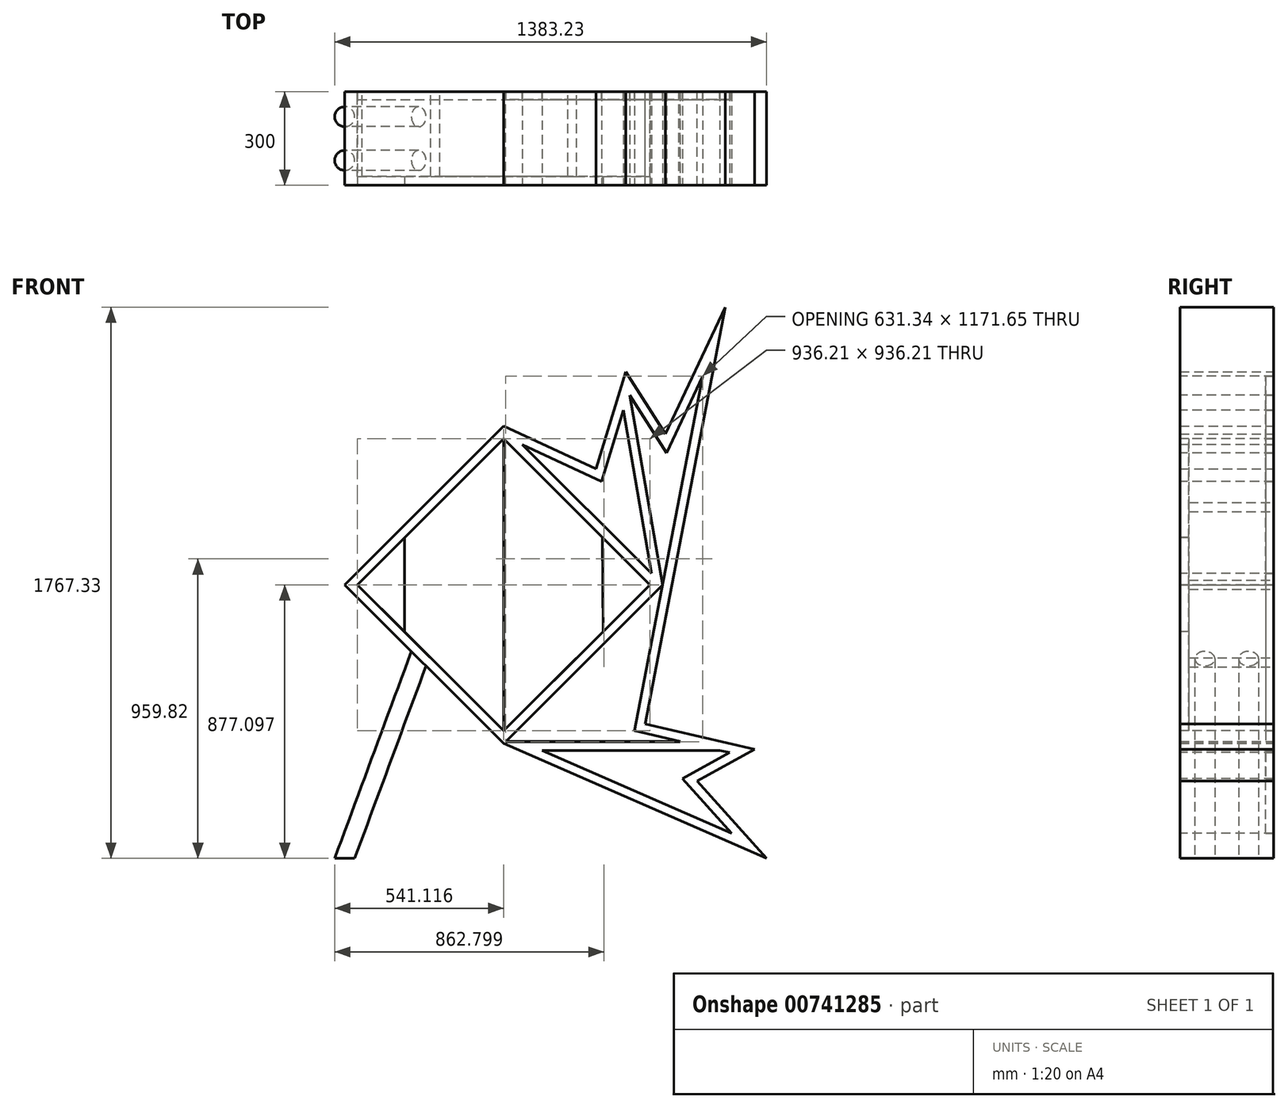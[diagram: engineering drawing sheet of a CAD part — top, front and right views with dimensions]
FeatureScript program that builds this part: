
annotation { "Feature Type Name" : "Feature", "Feature Type Description" : "" }
export const myFeature = defineFeature(function(context is Context, id is Id, definition is map)
    precondition{}
    {
        {
            var Q0;
            Q0=qCreatedBy(makeId("Front.planeOp"),FACE);
            var sketch = newSketch(context, id + "F0", { "sketchPlane" : qUnion([Q0])});
            skLineSegment(sketch, "E0", {"start": v(-825.73, 89.76) * mm, "end": v(-316.61, 598.87) * mm});
            skLineSegment(sketch, "E1", {"start": v(192.5, 89.76) * mm, "end": v(-316.61, -419.36) * mm});
            skLineSegment(sketch, "E2", {"start": v(-316.61, -419.36) * mm, "end": v(-825.73, 89.76) * mm});
            skLineSegment(sketch, "E3", {"start": v(-316.61, 598.87) * mm, "end": v(-21.16, 461.1) * mm});
            skLineSegment(sketch, "E4", {"start": v(-21.16, 461.1) * mm, "end": v(74.16, 772.86) * mm});
            skLineSegment(sketch, "E5", {"start": v(74.16, 772.86) * mm, "end": v(201.44, 572.46) * mm});
            skLineSegment(sketch, "E6", {"start": v(145.6, -358.84) * mm, "end": v(487.14, -437.47) * mm});
            skLineSegment(sketch, "E7", {"start": v(487.14, -437.47) * mm, "end": v(302.49, -539.98) * mm});
            skLineSegment(sketch, "E8", {"start": v(302.49, -539.98) * mm, "end": v(525.5, -787.34) * mm});
            skLineSegment(sketch, "E9", {"start": v(-316.61, -419.36) * mm, "end": v(525.5, -787.34) * mm});
            skPoint(sketch, "E10.endSnap0", {"position": v(394.81, -488.72) * mm});
            skLineSegment(sketch, "E11", {"start": v(-825.73, 89.76) * mm, "end": v(-588.14, -147.83) * mm});
            skLineSegment(sketch, "E12", {"start": v(-825.73, 89.76) * mm, "end": v(-825.73, -787.34) * mm, "construction": true});
            skLineSegment(sketch, "E13", {"start": v(-566.21, -86.45) * mm, "end": v(-825.73, -787.34) * mm});
            skLineSegment(sketch, "E14", {"start": v(-784.72, 89.76) * mm, "end": v(-316.61, 557.86) * mm});
            skLineSegment(sketch, "E15", {"start": v(-316.61, 557.86) * mm, "end": v(151.5, 89.76) * mm});
            skLineSegment(sketch, "E16", {"start": v(-784.72, 89.76) * mm, "end": v(-316.61, -378.35) * mm});
            skLineSegment(sketch, "E17", {"start": v(-316.61, -378.35) * mm, "end": v(151.5, 89.76) * mm});
            skLineSegment(sketch, "E18", {"start": v(-256.66, 538.92) * mm, "end": v(-3.18, 420.72) * mm});
            skLineSegment(sketch, "E19", {"start": v(66.34, 648.1) * mm, "end": v(-3.18, 420.72) * mm});
            skLineSegment(sketch, "E20", {"start": v(156.9, 125.36) * mm, "end": v(66.34, 648.1) * mm});
            skLineSegment(sketch, "E21", {"start": v(392.79, 979.99) * mm, "end": v(136.4, -356.72) * mm});
            skLineSegment(sketch, "E22", {"start": v(201.44, 572.46) * mm, "end": v(392.79, 979.99) * mm});
            skPoint(sketch, "E23.startSnap0", {"position": v(297.11, 776.23) * mm});
            skLineSegment(sketch, "E24", {"start": v(205.26, 512.36) * mm, "end": v(320.74, 758.3) * mm});
            skLineSegment(sketch, "E25", {"start": v(320.74, 758.3) * mm, "end": v(102.46, -379.66) * mm});
            skLineSegment(sketch, "E26", {"start": v(407.01, -448.78) * mm, "end": v(256.54, -532.32) * mm});
            skLineSegment(sketch, "E27", {"start": v(256.54, -532.32) * mm, "end": v(414, -706.97) * mm});
            skPoint(sketch, "E27.endSnap0", {"position": v(414, -663.66) * mm});
            skLineSegment(sketch, "E28", {"start": v(87.04, 698.48) * mm, "end": v(192.5, 89.76) * mm});
            skLineSegment(sketch, "E29", {"start": v(-316.61, 598.87) * mm, "end": v(192.5, 89.76) * mm});
            skLineSegment(sketch, "E30", {"start": v(136.4, -356.72) * mm, "end": v(487.14, -437.47) * mm});
            skLineSegment(sketch, "E31", {"start": v(87.04, 698.48) * mm, "end": v(205.26, 512.36) * mm});
            skLineSegment(sketch, "E32", {"start": v(-301.62, -404.37) * mm, "end": v(-310.6, -413.34) * mm});
            skLineSegment(sketch, "E33", {"start": v(-310.6, -413.34) * mm, "end": v(248.8, -413.34) * mm});
            skLineSegment(sketch, "E34", {"start": v(102.46, -379.66) * mm, "end": v(248.8, -413.34) * mm});
            skLineSegment(sketch, "E35", {"start": v(379.97, -442.55) * mm, "end": v(-191.11, -442.55) * mm});
            skLineSegment(sketch, "E36", {"start": v(379.97, -442.55) * mm, "end": v(407.01, -448.78) * mm});
            skLineSegment(sketch, "E37", {"start": v(-191.11, -442.55) * mm, "end": v(414, -706.97) * mm});
            skSolve(sketch);
        }
        {
            var Q0;
            {var subQ1=sQuery(id+"F0.wireOp",EDGE,"E3");Q0=makeQuery(id+"F0.imprint","IMPRINT",FACE,{"disambiguationData":[TD([[makeQuery(id+"F0.imprint","IMPRINT",EDGE,{"derivedFrom":subQ1}),-1.0]])]});}
            var Q1;
            {var subQ1=sQuery(id+"F0.wireOp",EDGE,"E0");Q1=makeQuery(id+"F0.imprint","IMPRINT",FACE,{"disambiguationData":[TD([[makeQuery(id+"F0.imprint","IMPRINT",EDGE,{"derivedFrom":subQ1}),-1.0]])]});}
            var Q2;
            Q2=makeQuery(id+"F0.imprint","IMPRINT",FACE,{"disambiguationData":[TD([[makeQuery(id+"F0.imprint","IMPRINT",EDGE,{"derivedFrom":sQuery(id+"F0.wireOp",EDGE,"E14")}),-1.0]])]});
            var Q3;
            {var subQ0=sQuery(id+"F0.wireOp",EDGE,"E24");Q3=makeQuery(id+"F0.imprint","IMPRINT",FACE,{"disambiguationData":[TD([[makeQuery(id+"F0.imprint","IMPRINT",EDGE,{"derivedFrom":subQ0}),-1.0]])]});}
            var Q4;
            Q4=makeQuery(id+"F0.imprint","IMPRINT",FACE,{"disambiguationData":[TD([[makeQuery(id+"F0.imprint","IMPRINT",EDGE,{"derivedFrom":sQuery(id+"F0.wireOp",EDGE,"E26")}),-1.0]])]});
            var Q5;
            {var subQ4=sQuery(id+"F0.wireOp",EDGE,"E32");Q5=makeQuery(id+"F0.imprint","IMPRINT",FACE,{"disambiguationData":[TD([[makeQuery(id+"F0.imprint","IMPRINT",EDGE,{"derivedFrom":subQ4}),1.0]])]});}
            var Q6;
            {var subQ0=sQuery(id+"F0.wireOp",EDGE,"E18");Q6=makeQuery(id+"F0.imprint","IMPRINT",FACE,{"disambiguationData":[TD([[makeQuery(id+"F0.imprint","IMPRINT",EDGE,{"derivedFrom":subQ0}),-1.0]])]});}
            extrude(context, id + "F1", {"entities" : qUnion([Q0, Q1, Q2, Q3, Q4, Q5, Q6]), "depth" : 300 * mm, "offsetDistance" : 25 * mm});
        }
        {
            var Q0;
            Q0=makeQuery(id+"F1.opExtrude","CAP_FACE",FACE,{"disambiguationData":[OSD([sQuery(id+"F0.wireOp",EDGE,"E0"),sQuery(id+"F0.wireOp",EDGE,"E2"),sQuery(id+"F0.wireOp",EDGE,"E3"),sQuery(id+"F0.wireOp",EDGE,"E4"),sQuery(id+"F0.wireOp",EDGE,"E5"),sQuery(id+"F0.wireOp",EDGE,"E7"),sQuery(id+"F0.wireOp",EDGE,"E8"),sQuery(id+"F0.wireOp",EDGE,"E9"),sQuery(id+"F0.wireOp",EDGE,"E11"),sQuery(id+"F0.wireOp",EDGE,"E21"),sQuery(id+"F0.wireOp",EDGE,"E22"),sQuery(id+"F0.wireOp",EDGE,"E30")])],"isStart":false});
            var sketch = newSketch(context, id + "F2", { "sketchPlane" : qUnion([Q0])});
            skLineSegment(sketch, "E38", {"start": v(-784.72, 89.76) * mm, "end": v(-316.61, 557.86) * mm});
            skLineSegment(sketch, "E39", {"start": v(-784.72, 89.76) * mm, "end": v(-316.61, -378.35) * mm});
            skLineSegment(sketch, "E40", {"start": v(-316.61, -378.35) * mm, "end": v(151.5, 89.76) * mm});
            skLineSegment(sketch, "E41", {"start": v(-316.61, 557.86) * mm, "end": v(151.5, 89.76) * mm});
            skPoint(sketch, "E42.startSnap0", {"position": v(-168.89, 529.99) * mm});
            skLineSegment(sketch, "E43", {"start": v(-3.18, 420.72) * mm, "end": v(66.5, 648.65) * mm});
            skLineSegment(sketch, "E44", {"start": v(-256.66, 538.92) * mm, "end": v(-3.18, 420.72) * mm});
            skLineSegment(sketch, "E45", {"start": v(66.5, 648.65) * mm, "end": v(156.84, 125.43) * mm});
            skLineSegment(sketch, "E46", {"start": v(87.44, 697.85) * mm, "end": v(192.44, 89.7) * mm});
            skLineSegment(sketch, "E47", {"start": v(-256.66, 538.92) * mm, "end": v(156.84, 125.43) * mm});
            skLineSegment(sketch, "E48", {"start": v(87.44, 697.85) * mm, "end": v(205.26, 512.36) * mm});
            skLineSegment(sketch, "E49", {"start": v(205.26, 512.36) * mm, "end": v(320.74, 758.3) * mm});
            skLineSegment(sketch, "E50", {"start": v(192.44, 89.7) * mm, "end": v(-309.57, -412.31) * mm});
            skLineSegment(sketch, "E51", {"start": v(102.64, -378.71) * mm, "end": v(320.74, 758.3) * mm});
            skLineSegment(sketch, "E52", {"start": v(-193.95, -441.31) * mm, "end": v(375.58, -441.31) * mm});
            skLineSegment(sketch, "E53", {"start": v(-310.6, -412.25) * mm, "end": v(-310.27, -412.25) * mm});
            skLineSegment(sketch, "E54", {"start": v(102.64, -378.71) * mm, "end": v(248.61, -412.31) * mm});
            skLineSegment(sketch, "E55", {"start": v(-309.57, -412.31) * mm, "end": v(248.61, -412.31) * mm});
            skLineSegment(sketch, "E56", {"start": v(375.58, -441.31) * mm, "end": v(407.3, -448.62) * mm});
            skLineSegment(sketch, "E57", {"start": v(407.3, -448.62) * mm, "end": v(256.54, -532.32) * mm});
            skLineSegment(sketch, "E58", {"start": v(414, -706.97) * mm, "end": v(256.54, -532.32) * mm});
            skLineSegment(sketch, "E59", {"start": v(414, -706.97) * mm, "end": v(-193.95, -441.31) * mm});
            skSolve(sketch);
        }
        {
            var Q0;
            Q0 = qSketchRegion(id + "F2", true);
            extrude(context, id + "F3", {"entities" : qUnion([Q0]), "operationType" : NewBodyOperationType.REMOVE, "endBound" : BoundingType.THROUGH_ALL, "oppositeDirection" : true, "depth" : 250 * mm, "offsetDistance" : 25 * mm});
        }
        {
            var Q0;
            Q0=makeQuery(id+"F2.imprint","IMPRINT",FACE,{"disambiguationData":[TD([[makeQuery(id+"F2.imprint","IMPRINT",EDGE,{"derivedFrom":sQuery(id+"F2.wireOp",EDGE,"E38")}),1.0]])]});
            var sketch = newSketch(context, id + "F4", { "sketchPlane" : qUnion([Q0])});
            skLineSegment(sketch, "E60", {"start": v(-316.61, 557.86) * mm, "end": v(-316.61, -378.35) * mm});
            skLineSegment(sketch, "E61", {"start": v(-634.72, 239.76) * mm, "end": v(-634.72, -60.25) * mm});
            skLineSegment(sketch, "E62", {"start": v(0, 241.25) * mm, "end": v(1.5, -60.24) * mm});
            skLineSegment(sketch, "E63", {"start": v(-634.72, 239.76) * mm, "end": v(-784.72, 89.76) * mm});
            skLineSegment(sketch, "E64", {"start": v(-784.72, 89.76) * mm, "end": v(-634.72, -60.25) * mm});
            skLineSegment(sketch, "E65", {"start": v(0, 241.25) * mm, "end": v(151.5, 89.76) * mm});
            skLineSegment(sketch, "E66", {"start": v(151.5, 89.76) * mm, "end": v(1.5, -60.24) * mm});
            skLineSegment(sketch, "E67", {"start": v(-634.72, 239.76) * mm, "end": v(-316.61, 557.86) * mm});
            skLineSegment(sketch, "E68", {"start": v(0, 241.25) * mm, "end": v(-316.61, 557.86) * mm});
            skLineSegment(sketch, "E69", {"start": v(1.5, -60.24) * mm, "end": v(-316.61, -378.35) * mm});
            skLineSegment(sketch, "E70", {"start": v(-634.72, -60.25) * mm, "end": v(-316.61, -378.35) * mm});
            skSolve(sketch);
        }
        {
            var Q0;
            Q0=makeQuery(id+"F4.imprint","IMPRINT",FACE,{"disambiguationData":[TD([[makeQuery(id+"F4.imprint","IMPRINT",EDGE,{"derivedFrom":sQuery(id+"F4.wireOp",EDGE,"E60")}),-1.0]])]});
            var Q1;
            Q1=makeQuery(id+"F4.imprint","IMPRINT",FACE,{"disambiguationData":[TD([[makeQuery(id+"F4.imprint","IMPRINT",EDGE,{"derivedFrom":sQuery(id+"F4.wireOp",EDGE,"E62")}),1.0]])]});
            extrude(context, id + "F5", {"entities" : qUnion([Q0, Q1]), "oppositeDirection" : true, "depth" : 29 * mm, "offsetDistance" : 25 * mm});
        }
        {
            var Q0;
            Q0=qCreatedBy(makeId("Top.planeOp"),FACE);
            var sketch = newSketch(context, id + "F6", { "sketchPlane" : qUnion([Q0])});
            skLineSegment(sketch, "E71.bottom", {"start": v(411.08, 500.96) * mm, "end": v(525.5, 500.96) * mm});
            skLineSegment(sketch, "E71.top", {"start": v(411.08, 415.79) * mm, "end": v(525.5, 415.79) * mm});
            skLineSegment(sketch, "E71.left", {"start": v(411.08, 500.96) * mm, "end": v(411.08, 415.79) * mm});
            skLineSegment(sketch, "E71.right", {"start": v(525.5, 500.96) * mm, "end": v(525.5, 415.79) * mm});
            skSolve(sketch);
        }
        {
            var Q0;
            Q0 = qSketchRegion(id + "F6", true);
            extrude(context, id + "F7", {"entities" : qUnion([Q0]), "oppositeDirection" : true, "depth" : 787.34 * mm, "offsetDistance" : 25 * mm});
        }
        {
            var Q0;
            Q0=makeQuery(id+"F7.opExtrude","CAP_FACE",FACE,{"disambiguationData":[OSD([sQuery(id+"F6.wireOp",EDGE,"E71.bottom"),sQuery(id+"F6.wireOp",EDGE,"E71.top"),sQuery(id+"F6.wireOp",EDGE,"E71.left"),sQuery(id+"F6.wireOp",EDGE,"E71.right")])],"isStart":false});
            var sketch = newSketch(context, id + "F8", { "sketchPlane" : qUnion([Q0])});
            skLineSegment(sketch, "E72", {"start": v(-825.73, 300) * mm, "end": v(-825.73, 0) * mm, "construction": true});
            skCircle(sketch, "E73", {"center": v(-825.73, 220) * mm, "radius": 32 * mm});
            skLineSegment(sketch, "E74", {"start": v(-825.73, 220) * mm, "end": v(-604.76, 220) * mm, "construction": true});
            skCircle(sketch, "E75", {"center": v(-825.73, 80) * mm, "radius": 32 * mm});
            skLineSegment(sketch, "E76", {"start": v(-825.73, 80) * mm, "end": v(-600.47, 80) * mm, "construction": true});
            skSolve(sketch);
        }
        {
            var Q0;
            Q0=makeQuery(id+"F8.imprint","IMPRINT",FACE,{"disambiguationData":[TD([[makeQuery(id+"F8.imprint","IMPRINT",EDGE,{"derivedFrom":sQuery(id+"F8.wireOp",EDGE,"E73")}),1.0]])]});
            var Q1;
            Q1=makeQuery(id+"F8.imprint","IMPRINT",FACE,{"disambiguationData":[TD([[makeQuery(id+"F8.imprint","IMPRINT",EDGE,{"derivedFrom":sQuery(id+"F8.wireOp",EDGE,"E75")}),1.0]])]});
            var Q2;
            Q2=sQuery(id+"F0.wireOp",EDGE,"E13");
            sweep(context, id + "F9", {"profiles" : qUnion([Q0, Q1]), "path" : qUnion([Q2])});
        }
        {
            var Q0;
            Q0=makeQuery(id+"F7.opExtrude","SWEPT_BODY",BODY,{"disambiguationData":[OSD([sQuery(id+"F6.wireOp",EDGE,"E71.bottom"),sQuery(id+"F6.wireOp",EDGE,"E71.top"),sQuery(id+"F6.wireOp",EDGE,"E71.left"),sQuery(id+"F6.wireOp",EDGE,"E71.right")])]});
            deleteBodies(context, id + "F10", {"entities" : qUnion([Q0])});
        }
        {
            var Q0;
            Q0=makeQuery(id+"F4.imprint","IMPRINT",FACE,{"disambiguationData":[TD([[makeQuery(id+"F4.imprint","IMPRINT",EDGE,{"derivedFrom":sQuery(id+"F4.wireOp",EDGE,"E61")}),-1.0]])]});
            var Q1;
            Q1=makeQuery(id+"F4.imprint","IMPRINT",FACE,{"disambiguationData":[TD([[makeQuery(id+"F4.imprint","IMPRINT",EDGE,{"derivedFrom":sQuery(id+"F4.wireOp",EDGE,"E60")}),1.0]])]});
            extrude(context, id + "F11", {"entities" : qUnion([Q0, Q1]), "oppositeDirection" : true, "depth" : 29 * mm, "offsetDistance" : 25 * mm});
        }
        {
            var Q0;
            Q0=makeQuery(id+"F1.opExtrude","CAP_FACE",FACE,{"disambiguationData":[OSD([sQuery(id+"F0.wireOp",EDGE,"E0"),sQuery(id+"F0.wireOp",EDGE,"E2"),sQuery(id+"F0.wireOp",EDGE,"E3"),sQuery(id+"F0.wireOp",EDGE,"E4"),sQuery(id+"F0.wireOp",EDGE,"E5"),sQuery(id+"F0.wireOp",EDGE,"E7"),sQuery(id+"F0.wireOp",EDGE,"E8"),sQuery(id+"F0.wireOp",EDGE,"E9"),sQuery(id+"F0.wireOp",EDGE,"E11"),sQuery(id+"F0.wireOp",EDGE,"E21"),sQuery(id+"F0.wireOp",EDGE,"E22"),sQuery(id+"F0.wireOp",EDGE,"E30")])],"isStart":true});
            var sketch = newSketch(context, id + "F12", { "sketchPlane" : qUnion([Q0])});
            skLineSegment(sketch, "E77", {"start": v(514.34, -221.64) * mm, "end": v(704.6, -31.37) * mm});
            skLineSegment(sketch, "E78", {"start": v(704.6, -31.37) * mm, "end": v(444.93, 0) * mm});
            skLineSegment(sketch, "E79", {"start": v(444.93, 0) * mm, "end": v(514.34, -221.64) * mm});
            skSolve(sketch);
        }
        {
            var Q0;
            Q0 = qSketchRegion(id + "F12", true);
            extrude(context, id + "F13", {"entities" : qUnion([Q0]), "oppositeDirection" : true, "depth" : 1133 * mm, "offsetDistance" : 25 * mm});
        }
        {
            var Q0;
            Q0=makeQuery(id+"F13.opExtrude","SWEPT_BODY",BODY,{"disambiguationData":[OSD([sQuery(id+"F12.wireOp",EDGE,"E77"),sQuery(id+"F12.wireOp",EDGE,"E78"),sQuery(id+"F12.wireOp",EDGE,"E79")])]});
            var Q1;
            Q1=makeQuery(id+"F9.opSweep","SWEPT_BODY",BODY,{"disambiguationData":[OSD([sQuery(id+"F0.wireOp",EDGE,"E13"),sQuery(id+"F8.wireOp",EDGE,"E73")])]});
            var Q2;
            Q2=makeQuery(id+"F9.opSweep","SWEPT_BODY",BODY,{"disambiguationData":[OSD([sQuery(id+"F0.wireOp",EDGE,"E13"),sQuery(id+"F8.wireOp",EDGE,"E75")])]});
            booleanBodies(context, id + "F14", {"operationType" : BooleanOperationType.SUBTRACTION, "tools" : qUnion([Q0]), "targets" : qUnion([Q1, Q2])});
        }
        {
            var Q0;
            Q0=makeQuery(id+"F1.opExtrude","CAP_FACE",FACE,{"disambiguationData":[OSD([sQuery(id+"F0.wireOp",EDGE,"E0"),sQuery(id+"F0.wireOp",EDGE,"E2"),sQuery(id+"F0.wireOp",EDGE,"E3"),sQuery(id+"F0.wireOp",EDGE,"E4"),sQuery(id+"F0.wireOp",EDGE,"E5"),sQuery(id+"F0.wireOp",EDGE,"E7"),sQuery(id+"F0.wireOp",EDGE,"E8"),sQuery(id+"F0.wireOp",EDGE,"E9"),sQuery(id+"F0.wireOp",EDGE,"E11"),sQuery(id+"F0.wireOp",EDGE,"E21"),sQuery(id+"F0.wireOp",EDGE,"E22"),sQuery(id+"F0.wireOp",EDGE,"E30")])],"isStart":true});
            var sketch = newSketch(context, id + "F15", { "sketchPlane" : qUnion([Q0])});
            skLineSegment(sketch, "E80.0", {"start": v(316.61, 557.86) * mm, "end": v(-151.5, 89.76) * mm});
            skLineSegment(sketch, "E80.1", {"start": v(316.61, -378.35) * mm, "end": v(-151.5, 89.76) * mm});
            skLineSegment(sketch, "E80.2", {"start": v(784.72, 89.76) * mm, "end": v(316.61, -378.35) * mm});
            skLineSegment(sketch, "E80.3", {"start": v(784.72, 89.76) * mm, "end": v(316.61, 557.86) * mm});
            skLineSegment(sketch, "E80.4", {"start": v(309.57, -412.31) * mm, "end": v(-248.61, -412.31) * mm});
            skLineSegment(sketch, "E80.5", {"start": v(-192.44, 89.7) * mm, "end": v(309.57, -412.31) * mm});
            skLineSegment(sketch, "E80.6", {"start": v(-102.64, -378.71) * mm, "end": v(-320.74, 758.3) * mm});
            skLineSegment(sketch, "E80.7", {"start": v(-102.64, -378.71) * mm, "end": v(-248.61, -412.31) * mm});
            skLineSegment(sketch, "E80.8", {"start": v(-407.3, -448.62) * mm, "end": v(-256.54, -532.32) * mm});
            skLineSegment(sketch, "E80.9", {"start": v(193.95, -441.31) * mm, "end": v(-375.58, -441.31) * mm});
            skLineSegment(sketch, "E80.10", {"start": v(-414, -706.97) * mm, "end": v(193.95, -441.31) * mm});
            skLineSegment(sketch, "E80.11", {"start": v(-414, -706.97) * mm, "end": v(-256.54, -532.32) * mm});
            skLineSegment(sketch, "E80.12", {"start": v(-375.58, -441.31) * mm, "end": v(-407.3, -448.62) * mm});
            skLineSegment(sketch, "E80.13", {"start": v(-205.26, 512.36) * mm, "end": v(-320.74, 758.3) * mm});
            skLineSegment(sketch, "E80.14", {"start": v(-87.44, 697.85) * mm, "end": v(-205.26, 512.36) * mm});
            skLineSegment(sketch, "E80.15", {"start": v(-87.44, 697.85) * mm, "end": v(-192.44, 89.7) * mm});
            skLineSegment(sketch, "E80.16", {"start": v(-66.5, 648.65) * mm, "end": v(-156.84, 125.43) * mm});
            skLineSegment(sketch, "E80.17", {"start": v(3.18, 420.72) * mm, "end": v(-66.5, 648.65) * mm});
            skLineSegment(sketch, "E80.19", {"start": v(256.66, 538.92) * mm, "end": v(-156.84, 125.43) * mm});
            skLineSegment(sketch, "E81.0", {"start": v(256.66, 538.92) * mm, "end": v(3.18, 420.72) * mm});
            skSolve(sketch);
        }
        {
            var Q0;
            Q0 = qSketchRegion(id + "F15", true);
            extrude(context, id + "F16", {"entities" : qUnion([Q0]), "oppositeDirection" : true, "depth" : 25 * mm, "offsetDistance" : 25 * mm});
        }
        {
            var Q0;
            Q0=makeQuery(id+"F16.opExtrude","CAP_FACE",FACE,{"disambiguationData":[OSD([sQuery(id+"F15.wireOp",EDGE,"E80.0"),sQuery(id+"F15.wireOp",EDGE,"E80.1"),sQuery(id+"F15.wireOp",EDGE,"E80.2"),sQuery(id+"F15.wireOp",EDGE,"E80.3")])],"isStart":true});
            var sketch = newSketch(context, id + "F17", { "sketchPlane" : qUnion([Q0])});
            skLineSegment(sketch, "E82", {"start": v(-151.5, 89.76) * mm, "end": v(-137, 104.26) * mm});
            skLineSegment(sketch, "E83", {"start": v(-137, 104.26) * mm, "end": v(770.22, 104.26) * mm});
            skLineSegment(sketch, "E84", {"start": v(770.22, 104.26) * mm, "end": v(784.72, 89.76) * mm});
            skLineSegment(sketch, "E85", {"start": v(770.22, 75.26) * mm, "end": v(-137, 75.26) * mm});
            skLineSegment(sketch, "E86", {"start": v(-137, 75.26) * mm, "end": v(-151.5, 89.76) * mm});
            skLineSegment(sketch, "E87", {"start": v(111.56, -173.3) * mm, "end": v(521.67, -173.3) * mm});
            skLineSegment(sketch, "E88", {"start": v(550.67, -144.3) * mm, "end": v(82.56, -144.3) * mm});
            skLineSegment(sketch, "E89", {"start": v(82.56, -144.3) * mm, "end": v(111.56, -173.3) * mm});
            skLineSegment(sketch, "E90", {"start": v(82.56, 323.8) * mm, "end": v(550.67, 323.8) * mm});
            skLineSegment(sketch, "E91", {"start": v(550.67, 323.8) * mm, "end": v(521.67, 352.8) * mm});
            skLineSegment(sketch, "E92", {"start": v(521.67, 352.8) * mm, "end": v(111.56, 352.8) * mm});
            skLineSegment(sketch, "E93", {"start": v(111.56, 352.8) * mm, "end": v(82.56, 323.8) * mm});
            skSolve(sketch);
        }
        {
            var Q0;
            Q0 = qSketchRegion(id + "F17", true);
            var Q1;
            Q1=makeQuery(id+"F17.imprint","IMPRINT",FACE,{"disambiguationData":[TD([[makeQuery(id+"F17.imprint","IMPRINT",EDGE,{"derivedFrom":sQuery(id+"F17.wireOp",EDGE,"E82")}),1.0]])]});
            var Q2;
            {var subQ0=sQuery(id+"F17.wireOp",EDGE,"E87");Q2=makeQuery(id+"F17.imprint","IMPRINT",FACE,{"disambiguationData":[TD([[makeQuery(id+"F17.imprint","IMPRINT",EDGE,{"derivedFrom":subQ0}),1.0]])]});}
            extrude(context, id + "F18", {"entities" : qUnion([Q0, Q1, Q2]), "oppositeDirection" : true, "depth" : 271 * mm, "offsetDistance" : 25 * mm});
        }
    });
